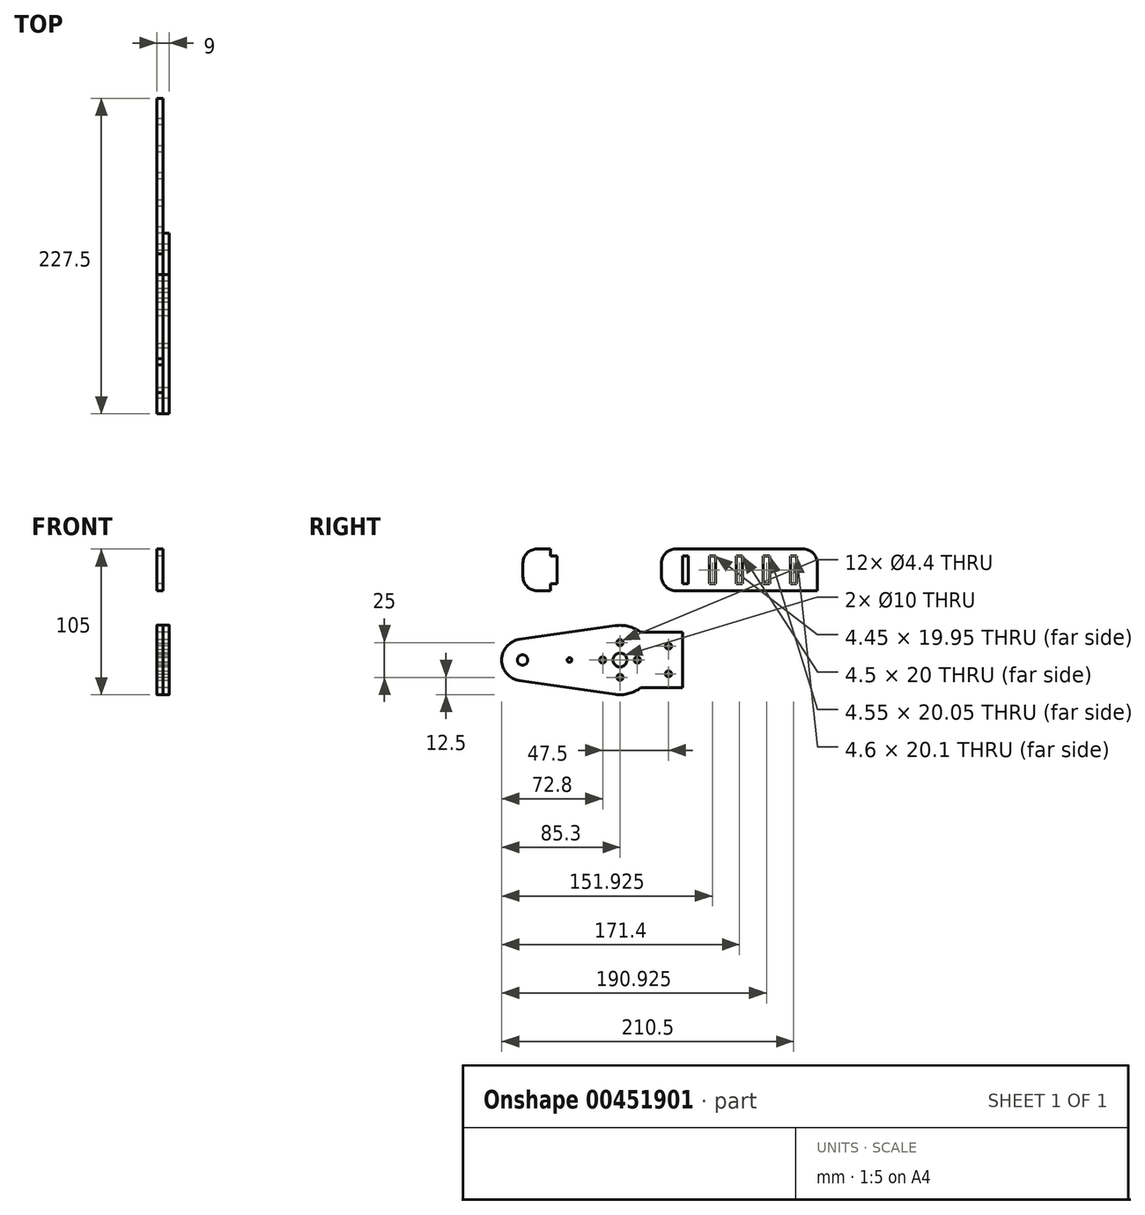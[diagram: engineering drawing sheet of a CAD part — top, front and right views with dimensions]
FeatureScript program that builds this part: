
annotation { "Feature Type Name" : "Feature", "Feature Type Description" : "" }
export const myFeature = defineFeature(function(context is Context, id is Id, definition is map)
    precondition{}
    {
        {
            var Q0;
            Q0=qCreatedBy(makeId("Right.planeOp"),FACE);
            var sketch = newSketch(context, id + "F0", { "sketchPlane" : qUnion([Q0])});
            skCircle(sketch, "E0", {"center": v(0, 0) * mm, "radius": 5 * mm});
            skCircle(sketch, "E1", {"center": v(-70.3, 0) * mm, "radius": 3.75 * mm});
            skCircle(sketch, "E2", {"center": v(-70.3, 0) * mm, "radius": 15 * mm});
            skCircle(sketch, "E3", {"center": v(0, 0) * mm, "radius": 25 * mm});
            skLineSegment(sketch, "E4", {"start": v(-72.43, 14.85) * mm, "end": v(-3.56, 24.75) * mm});
            skLineSegment(sketch, "E5", {"start": v(-72.43, -14.85) * mm, "end": v(-3.56, -24.75) * mm});
            skCircle(sketch, "E6", {"center": v(0, 0) * mm, "radius": 12.5 * mm, "construction": true});
            skPoint(sketch, "E7", {"position": v(0, 12.5) * mm});
            skPoint(sketch, "E8.1.0", {"position": v(-12.5, 0) * mm});
            skPoint(sketch, "E8.2.0", {"position": v(0, -12.5) * mm});
            skPoint(sketch, "E8.3.0", {"position": v(12.5, 0) * mm});
            skLineSegment(sketch, "E9", {"start": v(-70.3, 0) * mm, "end": v(-53.34, 0) * mm, "construction": true});
            skLineSegment(sketch, "E10", {"start": v(-53.34, 0) * mm, "end": v(-36.38, 0) * mm, "construction": true});
            skPoint(sketch, "E11", {"position": v(-53.34, 0) * mm});
            skPoint(sketch, "E12", {"position": v(-36.38, 0) * mm});
            skLineSegment(sketch, "E13", {"start": v(-36.38, 0) * mm, "end": v(-12.5, 0) * mm, "construction": true});
            skLineSegment(sketch, "E14", {"start": v(0, 0) * mm, "end": v(45, 0) * mm, "construction": true});
            skLineSegment(sketch, "E15", {"start": v(15, -20) * mm, "end": v(45, -20) * mm});
            skLineSegment(sketch, "E16", {"start": v(45, -20) * mm, "end": v(45, 20) * mm});
            skLineSegment(sketch, "E17", {"start": v(45, 20) * mm, "end": v(15, 20) * mm});
            skSolve(sketch);
        }
        {
            var Q0;
            Q0 = qSketchRegion(id + "F0", true);
            extrude(context, id + "F1", {"entities" : qUnion([Q0]), "depth" : 4.5 * mm, "offsetDistance" : 25 * mm});
        }
        {
            var Q0;
            Q0=sQuery(id+"F0.wireOp",VERTEX,"E8.1.0");
            var Q1;
            Q1=sQuery(id+"F0.wireOp",VERTEX,"E7");
            var Q2;
            Q2=sQuery(id+"F0.wireOp",VERTEX,"E8.2.0");
            var Q3;
            Q3=sQuery(id+"F0.wireOp",VERTEX,"E8.3.0");
            var Q4;
            Q4=makeQuery(id+"F1.opExtrude","SWEPT_BODY",BODY,{"disambiguationData":[OSD([sQuery(id+"F0.wireOp",EDGE,"E0"),sQuery(id+"F0.wireOp",EDGE,"E1"),sQuery(id+"F0.wireOp",EDGE,"E2"),sQuery(id+"F0.wireOp",EDGE,"E3"),sQuery(id+"F0.wireOp",EDGE,"E4"),sQuery(id+"F0.wireOp",EDGE,"E5")])]});
            hole(context, id + "F2", {"style" : HoleStyle.SIMPLE, "endStyle" : HoleEndStyle.BLIND, "oppositeDirection" : true, "standardTappedOrClearance" : lookupTablePath({ "standard" : "ISO", "fit" : "Normal", "size" : "M4", "type" : "Clearance" }), "standardBlindInLast" : lookupTablePath({ "fit" : "Standard", "standard" : "ISO", "size" : "M4", "type" : "Clearance" }), "holeDiameter" : 4.4 * mm, "holeDepth" : 20 * mm, "tappedDepth" : 12 * mm, "tapClearance" : 3, "locations" : qUnion([Q0, Q1, Q2, Q3]), "scope" : qUnion([Q4])});
        }
        {
            var Q0;
            Q0=qCreatedBy(makeId("Right.planeOp"),FACE);
            var sketch = newSketch(context, id + "F3", { "sketchPlane" : qUnion([Q0])});
            skLineSegment(sketch, "E18.bottom", {"start": v(-70, 50) * mm, "end": v(-50, 50) * mm});
            skLineSegment(sketch, "E18.top", {"start": v(-70, 80) * mm, "end": v(-50, 80) * mm});
            skLineSegment(sketch, "E18.left", {"start": v(-70, 50) * mm, "end": v(-70, 80) * mm});
            skLineSegment(sketch, "E18.right", {"start": v(-50, 50) * mm, "end": v(-50, 80) * mm});
            skPoint(sketch, "E18.middle", {"position": v(-60, 65) * mm});
            skLineSegment(sketch, "E19.bottom", {"start": v(-50, 75) * mm, "end": v(-45.5, 75) * mm});
            skLineSegment(sketch, "E19.top", {"start": v(-50, 55) * mm, "end": v(-45.5, 55) * mm});
            skLineSegment(sketch, "E19.left", {"start": v(-50, 75) * mm, "end": v(-50, 55) * mm});
            skLineSegment(sketch, "E19.right", {"start": v(-45.5, 75) * mm, "end": v(-45.5, 55) * mm});
            skPoint(sketch, "E19.middle", {"position": v(-47.75, 65) * mm});
            skLineSegment(sketch, "E20.bottom", {"start": v(30, 50) * mm, "end": v(142.2, 50) * mm});
            skLineSegment(sketch, "E20.top", {"start": v(30, 80) * mm, "end": v(142.2, 80) * mm});
            skLineSegment(sketch, "E20.left", {"start": v(30, 50) * mm, "end": v(30, 80) * mm});
            skLineSegment(sketch, "E20.right", {"start": v(142.2, 50) * mm, "end": v(142.2, 80) * mm});
            skPoint(sketch, "E20.middle", {"position": v(86.1, 65) * mm});
            skPoint(sketch, "E20.middle.positionSnap0", {"position": v(-45.5, 65) * mm});
            skPoint(sketch, "E20.centerSnap0", {"position": v(-45.5, 65) * mm});
            skLineSegment(sketch, "E21.bottom", {"start": v(49.4, 55.05) * mm, "end": v(45, 55.05) * mm});
            skLineSegment(sketch, "E21.top", {"start": v(49.4, 74.95) * mm, "end": v(45, 74.95) * mm});
            skLineSegment(sketch, "E21.left", {"start": v(49.4, 55.05) * mm, "end": v(49.4, 74.95) * mm});
            skLineSegment(sketch, "E21.right", {"start": v(45, 55.05) * mm, "end": v(45, 74.95) * mm});
            skPoint(sketch, "E21.middle", {"position": v(47.2, 65) * mm});
            skLineSegment(sketch, "E22.bottom", {"start": v(68.85, 55.03) * mm, "end": v(64.4, 55.03) * mm});
            skLineSegment(sketch, "E22.top", {"start": v(68.85, 74.97) * mm, "end": v(64.4, 74.97) * mm});
            skLineSegment(sketch, "E22.left", {"start": v(68.85, 55.03) * mm, "end": v(68.85, 74.97) * mm});
            skLineSegment(sketch, "E22.right", {"start": v(64.4, 55.02) * mm, "end": v(64.4, 74.98) * mm});
            skPoint(sketch, "E22.middle", {"position": v(66.62, 65) * mm});
            skLineSegment(sketch, "E23.bottom", {"start": v(88.35, 55) * mm, "end": v(83.85, 55) * mm});
            skLineSegment(sketch, "E23.top", {"start": v(88.35, 75) * mm, "end": v(83.85, 75) * mm});
            skLineSegment(sketch, "E23.left", {"start": v(88.35, 55) * mm, "end": v(88.35, 75) * mm});
            skLineSegment(sketch, "E23.right", {"start": v(83.85, 55) * mm, "end": v(83.85, 75) * mm});
            skLineSegment(sketch, "E24.bottom", {"start": v(107.9, 54.98) * mm, "end": v(103.35, 54.98) * mm});
            skLineSegment(sketch, "E24.top", {"start": v(107.9, 75.03) * mm, "end": v(103.35, 75.03) * mm});
            skLineSegment(sketch, "E24.left", {"start": v(107.9, 54.97) * mm, "end": v(107.9, 75.03) * mm});
            skLineSegment(sketch, "E24.right", {"start": v(103.35, 54.97) * mm, "end": v(103.35, 75.03) * mm});
            skPoint(sketch, "E24.middle", {"position": v(105.63, 65) * mm});
            skLineSegment(sketch, "E25.bottom", {"start": v(127.5, 54.95) * mm, "end": v(122.9, 54.95) * mm});
            skLineSegment(sketch, "E25.top", {"start": v(127.5, 75.05) * mm, "end": v(122.9, 75.05) * mm});
            skLineSegment(sketch, "E25.left", {"start": v(127.5, 54.95) * mm, "end": v(127.5, 75.05) * mm});
            skLineSegment(sketch, "E25.right", {"start": v(122.9, 54.95) * mm, "end": v(122.9, 75.05) * mm});
            skPoint(sketch, "E25.middle", {"position": v(125.2, 65) * mm});
            skLineSegment(sketch, "E26", {"start": v(30, 65) * mm, "end": v(45, 65) * mm, "construction": true});
            skLineSegment(sketch, "E27", {"start": v(49.4, 65) * mm, "end": v(64.4, 65) * mm, "construction": true});
            skLineSegment(sketch, "E28", {"start": v(68.85, 65) * mm, "end": v(83.85, 65) * mm, "construction": true});
            skLineSegment(sketch, "E29", {"start": v(88.35, 65) * mm, "end": v(103.35, 65) * mm, "construction": true});
            skLineSegment(sketch, "E30", {"start": v(107.9, 65) * mm, "end": v(122.9, 65) * mm, "construction": true});
            skLineSegment(sketch, "E31", {"start": v(127.5, 65) * mm, "end": v(142.2, 65) * mm, "construction": true});
            skSolve(sketch);
        }
        {
            var Q0;
            Q0 = qSketchRegion(id + "F3", true);
            extrude(context, id + "F4", {"entities" : qUnion([Q0]), "depth" : 4.5 * mm, "offsetDistance" : 25 * mm});
        }
        {
            var Q0;
            Q0=makeQuery(id+"F4.opExtrude","SWEPT_EDGE",EDGE,{"disambiguationData":[OSD([sQuery(id+"F3.wireOp",EDGE,"E18.bottom"),sQuery(id+"F3.wireOp",EDGE,"E18.left")])]});
            var Q1;
            Q1=makeQuery(id+"F4.opExtrude","SWEPT_EDGE",EDGE,{"disambiguationData":[OSD([sQuery(id+"F3.wireOp",EDGE,"E18.top"),sQuery(id+"F3.wireOp",EDGE,"E18.left")])]});
            var Q2;
            Q2=makeQuery(id+"F4.opExtrude","SWEPT_EDGE",EDGE,{"disambiguationData":[OSD([sQuery(id+"F3.wireOp",EDGE,"E20.top"),sQuery(id+"F3.wireOp",EDGE,"E20.left")])]});
            var Q3;
            Q3=makeQuery(id+"F4.opExtrude","SWEPT_EDGE",EDGE,{"disambiguationData":[OSD([sQuery(id+"F3.wireOp",EDGE,"E20.bottom"),sQuery(id+"F3.wireOp",EDGE,"E20.left")])]});
            var Q4;
            Q4=makeQuery(id+"F4.opExtrude","SWEPT_EDGE",EDGE,{"disambiguationData":[OSD([sQuery(id+"F3.wireOp",EDGE,"E20.top"),sQuery(id+"F3.wireOp",EDGE,"E20.right")])]});
            fillet(context, id + "F5", {"entities" : qUnion([Q0, Q1, Q2, Q3, Q4]), "radius" : 10 * mm, "tangentPropagation" : true, "allowEdgeOverflow" : false});
        }
        {
            var Q0;
            Q0=makeQuery(id+"F1.opExtrude","CAP_FACE",FACE,{"disambiguationData":[OSD([sQuery(id+"F0.wireOp",EDGE,"E0"),sQuery(id+"F0.wireOp",EDGE,"E1"),sQuery(id+"F0.wireOp",EDGE,"E2"),sQuery(id+"F0.wireOp",EDGE,"E3"),sQuery(id+"F0.wireOp",EDGE,"E4"),sQuery(id+"F0.wireOp",EDGE,"E5")])],"isStart":false});
            var sketch = newSketch(context, id + "F6", { "sketchPlane" : qUnion([Q0])});
            skArc(sketch, "E32.0.0", {"start": v(15, 20) * mm, "mid": v(6.2, 24.22) * mm, "end": v(-3.56, 24.75) * mm});
            skLineSegment(sketch, "E32.0.1", {"start": v(-3.56, 24.75) * mm, "end": v(-72.43, 14.85) * mm});
            skArc(sketch, "E32.0.2", {"start": v(-72.43, 14.85) * mm, "mid": v(-85.3, 0) * mm, "end": v(-72.43, -14.85) * mm});
            skLineSegment(sketch, "E32.0.3", {"start": v(-72.43, -14.85) * mm, "end": v(-3.56, -24.75) * mm});
            skCircle(sketch, "E33.0", {"center": v(0, -12.5) * mm, "radius": 2.2 * mm});
            skCircle(sketch, "E34.0", {"center": v(-12.5, 0) * mm, "radius": 2.2 * mm});
            skCircle(sketch, "E35.0", {"center": v(0, 0) * mm, "radius": 5 * mm});
            skCircle(sketch, "E36.0", {"center": v(12.5, 0) * mm, "radius": 2.2 * mm});
            skCircle(sketch, "E37.0", {"center": v(0, 12.5) * mm, "radius": 2.2 * mm});
            skCircle(sketch, "E38", {"center": v(-70.3, 0) * mm, "radius": 3.75 * mm});
            skLineSegment(sketch, "E39.0", {"start": v(15, -20) * mm, "end": v(45, -20) * mm});
            skLineSegment(sketch, "E40.0.0", {"start": v(45, 20) * mm, "end": v(15, 20) * mm});
            skLineSegment(sketch, "E40.0.7", {"start": v(45, -20) * mm, "end": v(45, 20) * mm});
            skArc(sketch, "E41.trimOffspring", {"start": v(-3.56, -24.75) * mm, "mid": v(6.2, -24.22) * mm, "end": v(15, -20) * mm});
            skSolve(sketch);
        }
        {
            var Q0;
            Q0 = qSketchRegion(id + "F6", true);
            extrude(context, id + "F7", {"entities" : qUnion([Q0]), "depth" : 4.5 * mm, "offsetDistance" : 25 * mm});
        }
        {
            var Q0;
            Q0=sQuery(id+"F0.wireOp",VERTEX,"E12");
            var Q1;
            Q1=makeQuery(id+"F1.opExtrude","SWEPT_BODY",BODY,{"disambiguationData":[OSD([sQuery(id+"F0.wireOp",EDGE,"E0"),sQuery(id+"F0.wireOp",EDGE,"E1"),sQuery(id+"F0.wireOp",EDGE,"E2"),sQuery(id+"F0.wireOp",EDGE,"E3"),sQuery(id+"F0.wireOp",EDGE,"E4"),sQuery(id+"F0.wireOp",EDGE,"E5"),sQuery(id+"F0.wireOp",EDGE,"E15"),sQuery(id+"F0.wireOp",EDGE,"E16"),sQuery(id+"F0.wireOp",EDGE,"E17")])]});
            var Q2;
            Q2=makeQuery(id+"F7.opExtrude","SWEPT_BODY",BODY,{"disambiguationData":[OSD([sQuery(id+"F6.wireOp",EDGE,"E33.0"),sQuery(id+"F6.wireOp",EDGE,"E34.0"),sQuery(id+"F6.wireOp",EDGE,"E35.0"),sQuery(id+"F6.wireOp",EDGE,"E36.0"),sQuery(id+"F6.wireOp",EDGE,"E37.0"),sQuery(id+"F6.wireOp",EDGE,"E38"),sQuery(id+"F6.wireOp",EDGE,"E40.0.0"),sQuery(id+"F6.wireOp",EDGE,"E32.0.1"),sQuery(id+"F6.wireOp",EDGE,"E32.0.2"),sQuery(id+"F6.wireOp",EDGE,"E32.0.3"),sQuery(id+"F6.wireOp",EDGE,"E32.0.0"),sQuery(id+"F6.wireOp",EDGE,"E39.0"),sQuery(id+"F6.wireOp",EDGE,"E40.0.7"),sQuery(id+"F6.wireOp",EDGE,"E41.trimOffspring")])]});
            hole(context, id + "F8", {"style" : HoleStyle.SIMPLE, "endStyle" : HoleEndStyle.BLIND, "oppositeDirection" : true, "standardTappedOrClearance" : lookupTablePath({ "standard" : "ISO", "fit" : "Normal", "size" : "M3", "type" : "Clearance" }), "standardBlindInLast" : lookupTablePath({ "fit" : "Standard", "standard" : "ISO", "size" : "M3", "type" : "Clearance" }), "holeDiameter" : 3.3 * mm, "holeDepth" : 20 * mm, "tappedDepth" : 12 * mm, "tapClearance" : 3, "locations" : qUnion([Q0]), "scope" : qUnion([Q1, Q2])});
        }
        {
            var Q0;
            Q0=makeQuery(id+"F7.opExtrude","CAP_FACE",FACE,{"disambiguationData":[OSD([sQuery(id+"F6.wireOp",EDGE,"E33.0"),sQuery(id+"F6.wireOp",EDGE,"E34.0"),sQuery(id+"F6.wireOp",EDGE,"E35.0"),sQuery(id+"F6.wireOp",EDGE,"E36.0"),sQuery(id+"F6.wireOp",EDGE,"E37.0"),sQuery(id+"F6.wireOp",EDGE,"E38"),sQuery(id+"F6.wireOp",EDGE,"E40.0.0"),sQuery(id+"F6.wireOp",EDGE,"E32.0.1"),sQuery(id+"F6.wireOp",EDGE,"E32.0.2"),sQuery(id+"F6.wireOp",EDGE,"E32.0.3"),sQuery(id+"F6.wireOp",EDGE,"E32.0.0"),sQuery(id+"F6.wireOp",EDGE,"E39.0"),sQuery(id+"F6.wireOp",EDGE,"E40.0.7"),sQuery(id+"F6.wireOp",EDGE,"E41.trimOffspring")])],"isStart":false});
            var sketch = newSketch(context, id + "F9", { "sketchPlane" : qUnion([Q0])});
            skPoint(sketch, "E42.0", {"position": v(35, 20) * mm});
            skPoint(sketch, "E43.0", {"position": v(30, -20) * mm});
            skPoint(sketch, "E44", {"position": v(35, 10) * mm});
            skPoint(sketch, "E45", {"position": v(35, -10) * mm});
            skLineSegment(sketch, "E46", {"start": v(45, 0) * mm, "end": v(35, 0) * mm, "construction": true});
            skLineSegment(sketch, "E47", {"start": v(35, 20) * mm, "end": v(35, 0) * mm, "construction": true});
            skSolve(sketch);
        }
        {
            var Q0;
            Q0=sQuery(id+"F9.wireOp",VERTEX,"E45");
            var Q1;
            Q1=sQuery(id+"F9.wireOp",VERTEX,"E44");
            var Q2;
            Q2=makeQuery(id+"F1.opExtrude","SWEPT_BODY",BODY,{"disambiguationData":[OSD([sQuery(id+"F0.wireOp",EDGE,"E0"),sQuery(id+"F0.wireOp",EDGE,"E1"),sQuery(id+"F0.wireOp",EDGE,"E2"),sQuery(id+"F0.wireOp",EDGE,"E3"),sQuery(id+"F0.wireOp",EDGE,"E4"),sQuery(id+"F0.wireOp",EDGE,"E5"),sQuery(id+"F0.wireOp",EDGE,"E15"),sQuery(id+"F0.wireOp",EDGE,"E16"),sQuery(id+"F0.wireOp",EDGE,"E17")])]});
            var Q3;
            Q3=makeQuery(id+"F7.opExtrude","SWEPT_BODY",BODY,{"disambiguationData":[OSD([sQuery(id+"F6.wireOp",EDGE,"E33.0"),sQuery(id+"F6.wireOp",EDGE,"E34.0"),sQuery(id+"F6.wireOp",EDGE,"E35.0"),sQuery(id+"F6.wireOp",EDGE,"E36.0"),sQuery(id+"F6.wireOp",EDGE,"E37.0"),sQuery(id+"F6.wireOp",EDGE,"E38"),sQuery(id+"F6.wireOp",EDGE,"E40.0.0"),sQuery(id+"F6.wireOp",EDGE,"E32.0.1"),sQuery(id+"F6.wireOp",EDGE,"E32.0.2"),sQuery(id+"F6.wireOp",EDGE,"E32.0.3"),sQuery(id+"F6.wireOp",EDGE,"E32.0.0"),sQuery(id+"F6.wireOp",EDGE,"E39.0"),sQuery(id+"F6.wireOp",EDGE,"E40.0.7"),sQuery(id+"F6.wireOp",EDGE,"E41.trimOffspring")])]});
            hole(context, id + "F10", {"style" : HoleStyle.SIMPLE, "endStyle" : HoleEndStyle.BLIND, "standardTappedOrClearance" : lookupTablePath({ "standard" : "ISO", "fit" : "Normal", "size" : "M4", "type" : "Clearance" }), "standardBlindInLast" : lookupTablePath({ "fit" : "Standard", "standard" : "ISO", "size" : "M4", "type" : "Clearance" }), "holeDiameter" : 4.4 * mm, "holeDepth" : 20 * mm, "tappedDepth" : 12 * mm, "tapClearance" : 3, "locations" : qUnion([Q0, Q1]), "scope" : qUnion([Q2, Q3])});
        }
    });
